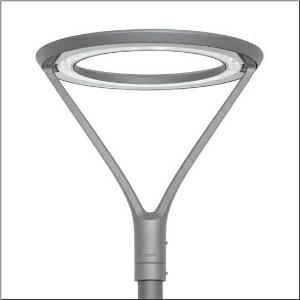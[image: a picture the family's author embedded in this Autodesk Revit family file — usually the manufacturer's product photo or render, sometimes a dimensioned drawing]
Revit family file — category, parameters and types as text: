
# Revit family: dl_r__20___st1_2a_5xa512836a008_c857
name_source: partatom
category: Lighting Fixtures
units: mm (PartAtom-declared; Revit-internal decimal feet)

## family parameters
Cut with Voids When Loaded = No
Host = Face
Light Source = No
Part Type = Normal
Room Calculation Point = No
Round Connector Dimension = Use Diameter
Shared = No

## types (1)
- --- (1 x LED, 3020 lm, 28.6 W, 2700K)
    Apparent Load = 29 VA
    CIE Flux Codes = 32 72 97 100 100
    Color Rendering = 70
    Color Temperature = 2700K
    Default Elevation = 1800 mm
    Description = DL® 20, mast luminaire, primary light control with reflector, highly specular, primary optical cover: cover, of toughened safety glass of clear glass with excellent transmission level, light distribution: ST1.2a, light emission: direct distribution, primary light characteristic: asymmetric, installation type: post-top, LED, High Power LED, rated luminous flux: 3.020lm, luminous efficacy: 106lm/W, light colour: 727, colour temperature: 2700K, control gear: Plus, control: flexible luminous flux parameterisation, time-dependent luminous flux control, constant luminous flux control, digital communication interface, power reduction, overheat protection, electronic power reduction, mains connection: 220..240V, 50/60Hz, connection cable pre-assembled, cable length: 5m, start of lifetime: 29W, end of service life: 29W, reduction: 15W, luminaire housing, upper part, of cast aluminium, powder-coated, Siteco® metallic grey (DB 702S), diameter: 690mm, height: 690mm, spigot size: 76mm (post-top), mounting height: 4..6m, luminaire housing, of cast aluminium, powder-coated, Siteco® metallic grey (DB 702S), equipment: standard, protection rating (complete): IP66, insulation class (complete): insulation class II (safety insulation), certification: CE, ENEC, VDE, impact resistance: IK08, permissible operating ambient temperature: -25..+35°C, standard-compliant lighting for roads and squares, packaging unit: 1 piece

Light Distribution: ST1.2a
    Height = 690 mm
    Lamp = 1 x LED
    Lamp Light Flux = 3020 lm
    Lamp Power = 28.6 W
    Lamp count = 1
    Length = 690 mm
    Luminous efficacy = 106 lm/W
    Manufacturer = Siteco
    ModVariant = No
    Model = 5XA512836A008
    Number of Poles = 1
    OnlyDefault = Yes
    Power Factor = 1
    Product Name = DL® 20 | ST1.2a
    Product group = mast luminaire | pylon top
    ProductGroupID = 6100
    Protection Class = Protection class II
    Protection Degree = IP 66
    RLX_Detail_Level = 1
    RLX_Emergency_Light_Flux = 0 lm
    RLX_Emergency_Type = 0
    RLX_Emergency_Type_DB = No
    RlxData = <blob elided: 206757 chars, md5=557fa7b0>
    Socket = socket
    Standby Power = 0 W
    System Light Flux = 3020 lm
    System Power = 29 W
    Type Comments = factory setting: luminous flux: 100 % | dim-lin: 254 | 386 mA
    Type Image = l_1006001.jpg
    URL = http://relux.com
    VarID = @adj_077348
    Voltage = 0 V
    Weight = 0.00 kg
    Width = 0 mm  [stored 0 ft]

note: [stored X ft] marks values corroborated as IEEE doubles in the binary element streams (Revit-internal decimal feet)

## geometry (parser evidence)
native form markers: Blend x4, Sweep x11
no freeform markers — native parametric forms only
